# Revit family: IS_Idealrain_Multiproduct_BIM_DE_B9501;B9503
name_source: partatom
category: Plumbing Fixtures
revit_build: Autodesk Revit MEP 2016 (Build: 20161004_0715(x64)
units: mm (PartAtom-declared; Revit-internal decimal feet)

## family parameters
Cut with Voids When Loaded = No
Host = Face
OmniClass Number = 23.45.05.14.17
OmniClass Title = Showers
Part Type = Normal
Room Calculation Point = No
Round Connector Dimension = Use Diameter
Shared = No

## types (2) — shared parameters
Accessories = www.idealstandard.de\ersatzteile
AreaUnits = millimeters
Assembly Code = C1030200
AssetType = Fixed
Brand = Ideal Standard
CodePerformance = 0
Color = Chrome
ConnectionType = Plumbing
CurrencyUnit = €
DurationUnit = year
ExpectedLife = 25
Finish = Chrome
InstallationDate = 1900-12-31T23:59:59
InstallationInstructions = www.idealstandard.de\produkte
LinearUnits = millimeters
ManufacturerURL = www.idealstandard.de
Material = Brass
NominalHeight = 606 mm
NominalLength = 184 mm
NominalWidth = 137 mm
ProductInformation = www.idealstandard.de
Shape = Sculptured
Size = 606 x 184 x 137 mm
Space = Internal
URL = www.idealstandard.de
Uniclass2015Code = Pr_40_20_87_75
Uniclass2015Title = Shower fittings package
Uniclass2015Version = Products v1.1
Version = 1
VolumeUnits = Litres
zero-valued in all types: Cost, Default Elevation, NominalDepth

## per-type parameters (varying)
| type | BIMObjectName | BarCode | Description | Features | GrossWeight | Model | ModelNumber | ModelReference | Name |
| B9501AA - IDEALRAIN S1 SPRCH.KOMB.1F/80 TYC 60CM | ISI_IdealStandard_Showers_IDEALRAIN_B9501AA | 3800861023753 | IDEALRAIN S1 SPRCH.KOMB.1F/80 TYC 60CM | IDEALRAIN shower kit with single function 80mm handspray, 600mm slide rail | 1,401 kg | B9501AA | B9501AA | IS Brausekombination IDEALRAIN 600mm 1-Funktionshandbrause d:80mm Chrom | ISI_IdealStandard_Showers_IDEALRAIN_B9501AA |
| B9503AA - IDEALRAIN S3 SPRCH.KOMB. 3F/80 TYC 60CM | ISI_IdealStandard_Showers_IDEALRAIN_B9503AA | 3800861023814 | IDEALRAIN S3 SPRCH.KOMB. 3F/80 TYC 60CM | IDEALRAIN shower kit with 3 function 80mm handspray, 600mm slide rail | 1,391 kg | B9503AA | B9503AA | IS Brausekombination IDEALRAIN 600mm 3-Funktionshandbrause d:80mm Chrom | ISI_IdealStandard_Showers_IDEALRAIN_B9503AA |

## geometry (parser evidence)
native form markers: Blend x4, Sweep x2
no freeform markers — native parametric forms only
